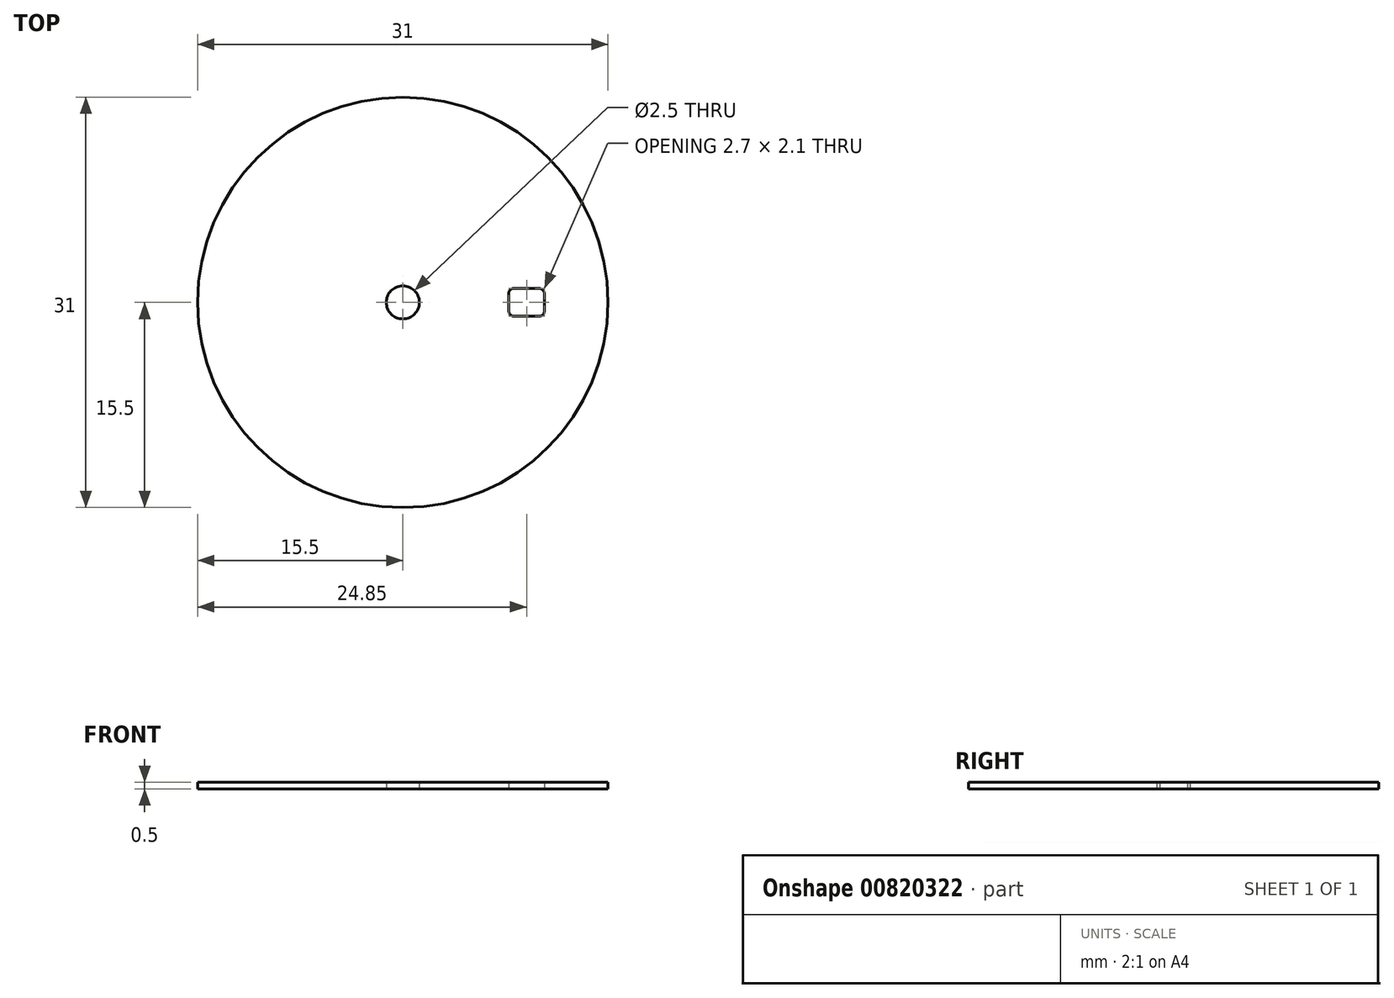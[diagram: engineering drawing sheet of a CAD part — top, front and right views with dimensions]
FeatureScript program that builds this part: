
annotation { "Feature Type Name" : "Feature", "Feature Type Description" : "" }
export const myFeature = defineFeature(function(context is Context, id is Id, definition is map)
    precondition{}
    {
        {
            var Q0;
            Q0=qCreatedBy(makeId("Top.planeOp"),FACE);
            var sketch = newSketch(context, id + "F0", { "sketchPlane" : qUnion([Q0])});
            skCircle(sketch, "E0", {"center": v(0, 0) * mm, "radius": 15.5 * mm});
            skCircle(sketch, "E1", {"center": v(0, 0) * mm, "radius": 1.25 * mm});
            skLineSegment(sketch, "E2.bottom", {"start": v(8.37, 1.05) * mm, "end": v(10.3, 1.05) * mm});
            skLineSegment(sketch, "E2.top", {"start": v(8.4, -1.05) * mm, "end": v(10.3, -1.05) * mm});
            skLineSegment(sketch, "E2.left", {"start": v(8, 0.68) * mm, "end": v(8, -0.65) * mm});
            skLineSegment(sketch, "E2.right", {"start": v(10.7, 0.65) * mm, "end": v(10.7, -0.65) * mm});
            skPoint(sketch, "E3.visualSharp", {"position": v(8, 1.05) * mm});
            skArc(sketch, "E3.filletArc", {"start": v(8.37, 1.05) * mm, "mid": v(8.1, 0.94) * mm, "end": v(8, 0.68) * mm});
            skPoint(sketch, "E4.visualSharp", {"position": v(10.7, 1.05) * mm});
            skArc(sketch, "E4.filletArc", {"start": v(10.7, 0.65) * mm, "mid": v(10.58, 0.93) * mm, "end": v(10.3, 1.05) * mm});
            skPoint(sketch, "E5.visualSharp", {"position": v(10.7, -1.05) * mm});
            skArc(sketch, "E5.filletArc", {"start": v(10.3, -1.05) * mm, "mid": v(10.58, -0.93) * mm, "end": v(10.7, -0.65) * mm});
            skPoint(sketch, "E6.visualSharp", {"position": v(8, -1.05) * mm});
            skArc(sketch, "E6.filletArc", {"start": v(8, -0.65) * mm, "mid": v(8.12, -0.93) * mm, "end": v(8.4, -1.05) * mm});
            skSolve(sketch);
        }
        {
            var Q0;
            Q0 = qSketchRegion(id + "F0", true);
            extrude(context, id + "F1", {"entities" : qUnion([Q0]), "depth" : 0.5 * mm, "offsetDistance" : 25 * mm});
        }
    });
